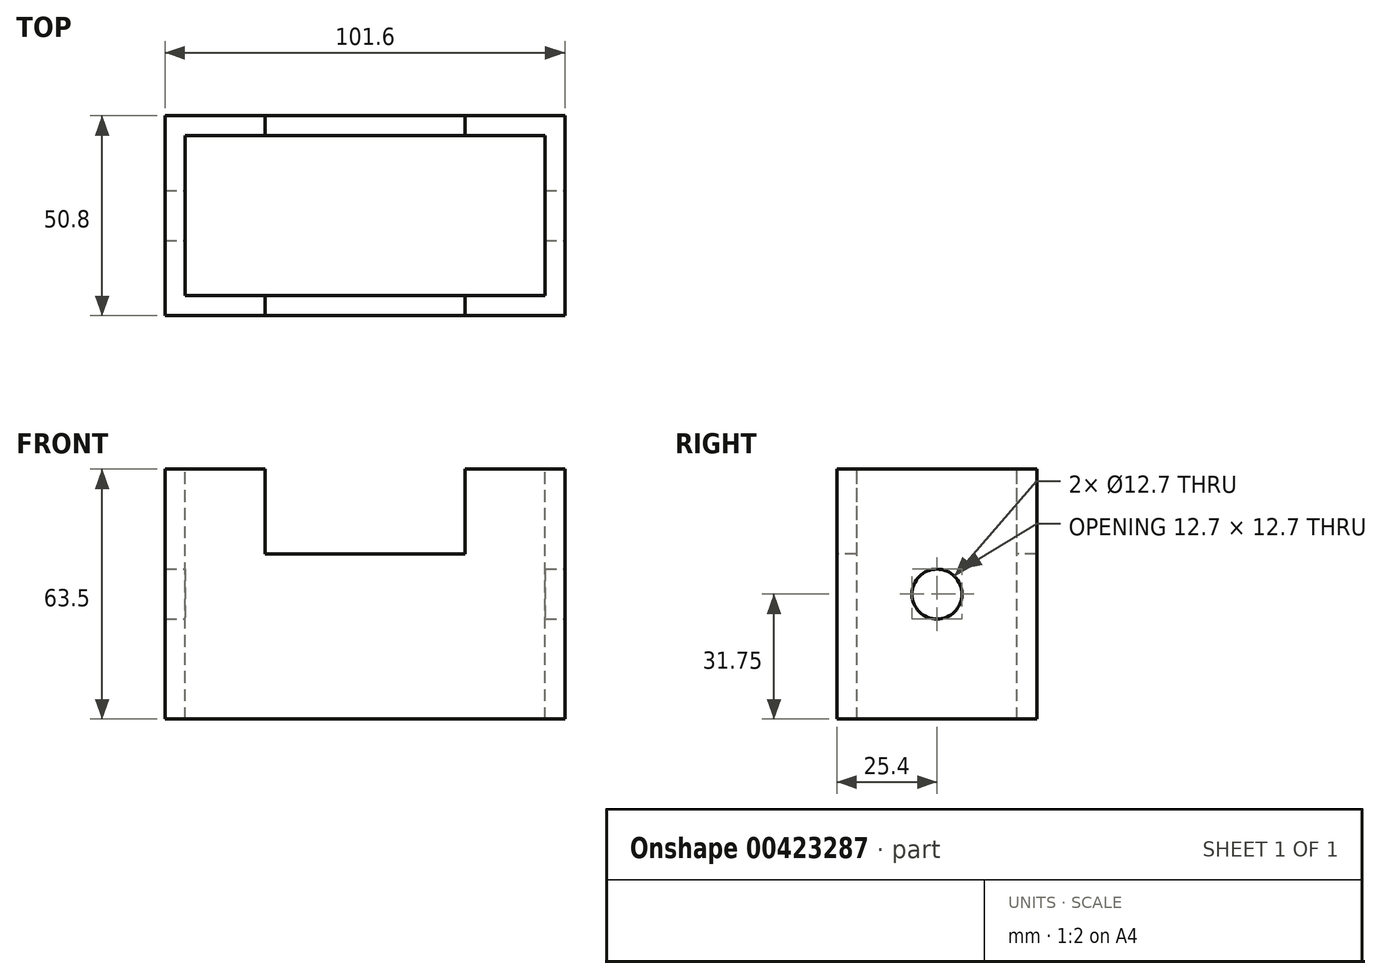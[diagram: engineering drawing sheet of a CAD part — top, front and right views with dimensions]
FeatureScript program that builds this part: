
annotation { "Feature Type Name" : "Feature", "Feature Type Description" : "" }
export const myFeature = defineFeature(function(context is Context, id is Id, definition is map)
    precondition{}
    {
        {
            var Q0;
            Q0=qCreatedBy(makeId("Front.planeOp"),FACE);
            var sketch = newSketch(context, id + "F0", { "sketchPlane" : qUnion([Q0])});
            skLineSegment(sketch, "E0.bottom", {"start": v(-50.8, 31.75) * mm, "end": v(50.8, 31.75) * mm});
            skLineSegment(sketch, "E0.top", {"start": v(-50.8, -31.75) * mm, "end": v(50.8, -31.75) * mm});
            skLineSegment(sketch, "E0.left", {"start": v(-50.8, 31.75) * mm, "end": v(-50.8, -31.75) * mm});
            skLineSegment(sketch, "E0.right", {"start": v(50.8, 31.75) * mm, "end": v(50.8, -31.75) * mm});
            skSolve(sketch);
        }
        {
            var Q0;
            Q0 = qSketchRegion(id + "F0", true);
            extrude(context, id + "F1", {"entities" : qUnion([Q0]), "depth" : 50.8 * mm});
        }
        {
            var Q0;
            Q0=makeQuery(id+"F1.opExtrude","CAP_FACE",FACE,{"disambiguationData":[OSD([sQuery(id+"F0.wireOp",EDGE,"E0.bottom"),sQuery(id+"F0.wireOp",EDGE,"E0.top"),sQuery(id+"F0.wireOp",EDGE,"E0.left"),sQuery(id+"F0.wireOp",EDGE,"E0.right")])],"isStart":false});
            var sketch = newSketch(context, id + "F2", { "sketchPlane" : qUnion([Q0])});
            skLineSegment(sketch, "E1.bottom", {"start": v(-25.4, 31.75) * mm, "end": v(25.4, 31.75) * mm});
            skLineSegment(sketch, "E1.top", {"start": v(-25.4, 10.16) * mm, "end": v(25.4, 10.16) * mm});
            skLineSegment(sketch, "E1.left", {"start": v(-25.4, 31.75) * mm, "end": v(-25.4, 10.16) * mm});
            skLineSegment(sketch, "E1.right", {"start": v(25.4, 31.75) * mm, "end": v(25.4, 10.16) * mm});
            skSolve(sketch);
        }
        {
            var Q0;
            Q0 = qSketchRegion(id + "F2", true);
            extrude(context, id + "F3", {"entities" : qUnion([Q0]), "operationType" : NewBodyOperationType.REMOVE, "oppositeDirection" : true, "depth" : 70.87 * mm});
        }
        {
            var Q0;
            {var subQ1=sQuery(id+"F0.wireOp",EDGE,"E0.left");var subQ3=sQuery(id+"F0.wireOp",EDGE,"E0.bottom");Q0=makeQuery(id+"F3.boolean.opBoolean","SPLIT",FACE,{"disambiguationData":[TD([makeQuery(id+"F1.opExtrude","SWEPT_FACE",FACE,{"disambiguationData":[OSD([subQ1])]})])],"derivedFrom":makeQuery(id+"F1.opExtrude","SWEPT_FACE",FACE,{"disambiguationData":[OSD([subQ3])]})});}
            var sketch = newSketch(context, id + "F4", { "sketchPlane" : qUnion([Q0])});
            skLineSegment(sketch, "E2.bottom", {"start": v(-45.72, -5.08) * mm, "end": v(45.72, -5.08) * mm});
            skLineSegment(sketch, "E2.top", {"start": v(-45.72, -45.72) * mm, "end": v(45.72, -45.72) * mm});
            skLineSegment(sketch, "E2.left", {"start": v(-45.72, -5.08) * mm, "end": v(-45.72, -45.72) * mm});
            skLineSegment(sketch, "E2.right", {"start": v(45.72, -5.08) * mm, "end": v(45.72, -45.72) * mm});
            skSolve(sketch);
        }
        {
            var Q0;
            Q0 = qSketchRegion(id + "F4", true);
            extrude(context, id + "F5", {"entities" : qUnion([Q0]), "operationType" : NewBodyOperationType.REMOVE, "oppositeDirection" : true, "depth" : 71.63 * mm});
        }
        {
            var Q0;
            Q0=makeQuery(id+"F1.opExtrude","SWEPT_FACE",FACE,{"disambiguationData":[OSD([sQuery(id+"F0.wireOp",EDGE,"E0.right")])]});
            var sketch = newSketch(context, id + "F6", { "sketchPlane" : qUnion([Q0])});
            skCircle(sketch, "E3", {"center": v(-25.4, 0) * mm, "radius": 6.35 * mm});
            skPoint(sketch, "E4", {"position": v(-25.4, 31.75) * mm});
            skSolve(sketch);
        }
        {
            var Q0;
            Q0 = qSketchRegion(id + "F6", true);
            extrude(context, id + "F7", {"entities" : qUnion([Q0]), "operationType" : NewBodyOperationType.REMOVE, "oppositeDirection" : true, "depth" : 111.5 * mm});
        }
    });
